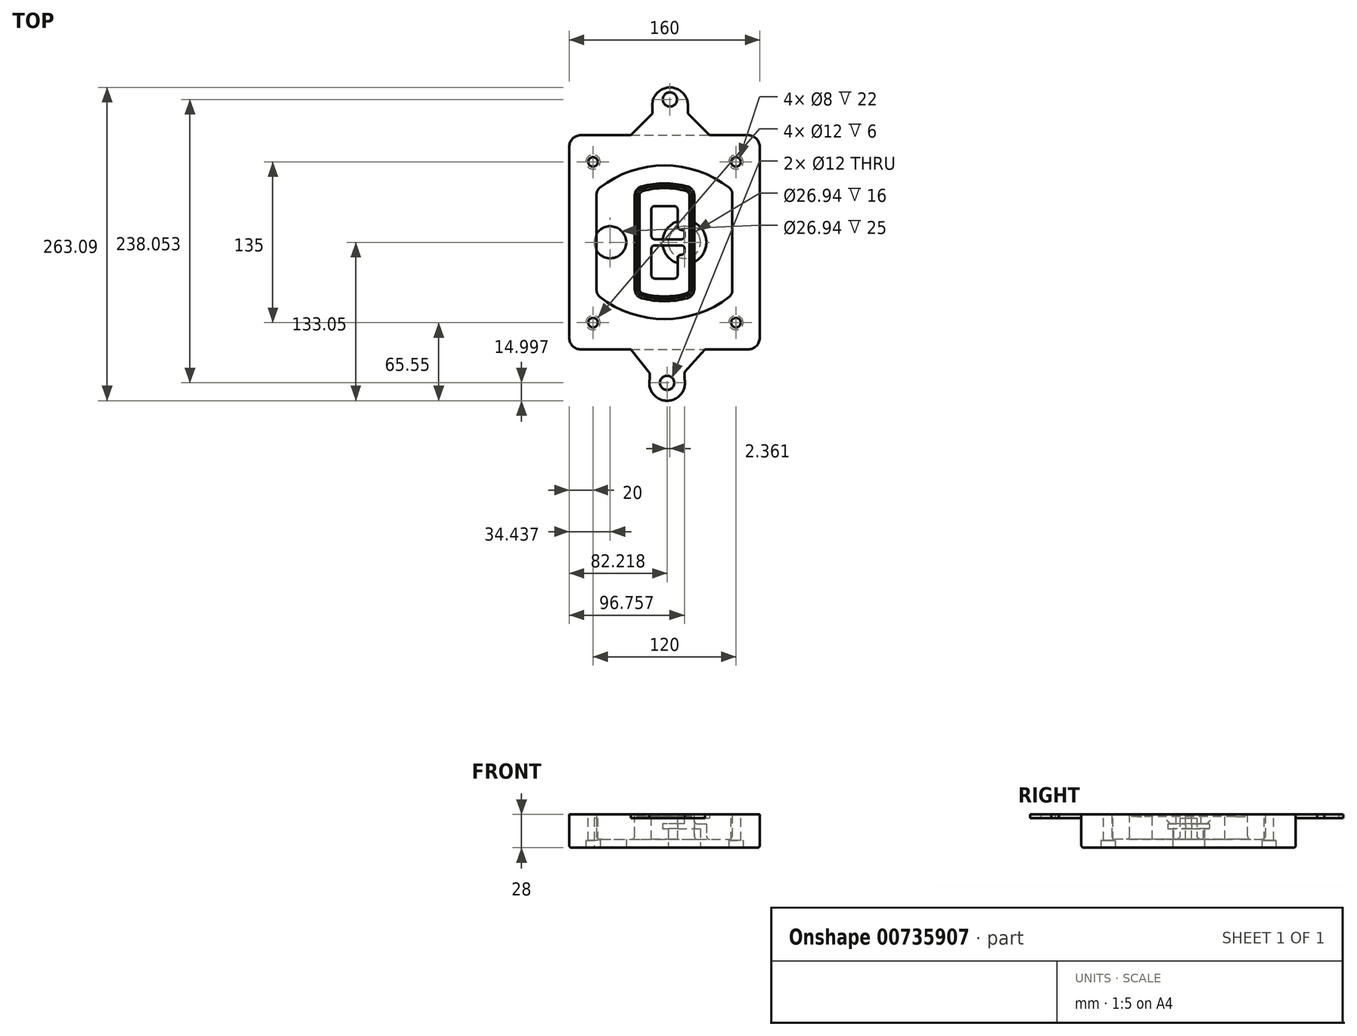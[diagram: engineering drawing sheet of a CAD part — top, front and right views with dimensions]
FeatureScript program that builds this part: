
annotation { "Feature Type Name" : "Feature", "Feature Type Description" : "" }
export const myFeature = defineFeature(function(context is Context, id is Id, definition is map)
    precondition{}
    {
        {
            var Q0;
            Q0=qCreatedBy(makeId("Top.planeOp"),FACE);
            var sketch = newSketch(context, id + "F0", { "sketchPlane" : qUnion([Q0])});
            skPoint(sketch, "E0.rect.middle", {"position": v(0, 0) * mm});
            skLineSegment(sketch, "E1.bottom", {"start": v(-70, -90) * mm, "end": v(70, -90) * mm});
            skLineSegment(sketch, "E1.top", {"start": v(-70, 90) * mm, "end": v(70, 90) * mm});
            skLineSegment(sketch, "E1.left", {"start": v(-80, -80) * mm, "end": v(-80, 80) * mm});
            skLineSegment(sketch, "E1.right", {"start": v(80, -80) * mm, "end": v(80, 80) * mm});
            skLineSegment(sketch, "E2", {"start": v(-80, 90) * mm, "end": v(80, -90) * mm, "construction": true});
            skLineSegment(sketch, "E3", {"start": v(80, 90) * mm, "end": v(-80, -90) * mm, "construction": true});
            skCircle(sketch, "E4", {"center": v(-60, 67.5) * mm, "radius": 4 * mm});
            skCircle(sketch, "E5", {"center": v(60, 67.5) * mm, "radius": 4 * mm});
            skCircle(sketch, "E6", {"center": v(60, -67.5) * mm, "radius": 4 * mm});
            skCircle(sketch, "E7", {"center": v(-60, -67.5) * mm, "radius": 4 * mm});
            skLineSegment(sketch, "E8", {"start": v(-60, 67.5) * mm, "end": v(60, 67.5) * mm, "construction": true});
            skLineSegment(sketch, "E9", {"start": v(60, 67.5) * mm, "end": v(60, -67.5) * mm, "construction": true});
            skLineSegment(sketch, "E10", {"start": v(60, -67.5) * mm, "end": v(-60, -67.5) * mm, "construction": true});
            skLineSegment(sketch, "E11", {"start": v(-60, -67.5) * mm, "end": v(-60, 67.5) * mm, "construction": true});
            skLineSegment(sketch, "E12", {"start": v(-60, 40.3) * mm, "end": v(-60, -40.3) * mm});
            skLineSegment(sketch, "E13", {"start": v(60, 40.3) * mm, "end": v(60, -40.3) * mm});
            skArc(sketch, "E14", {"start": v(56.15, 48.18) * mm, "mid": v(0, 67.5) * mm, "end": v(-56.15, 48.18) * mm});
            skArc(sketch, "E15", {"start": v(-56.15, -48.18) * mm, "mid": v(0, -67.5) * mm, "end": v(56.15, -48.18) * mm});
            skLineSegment(sketch, "E16", {"start": v(-60, 0) * mm, "end": v(60, 0) * mm, "construction": true});
            skPoint(sketch, "E17.visualSharp", {"position": v(-60, -45) * mm});
            skArc(sketch, "E17.filletArc", {"start": v(-60, -40.3) * mm, "mid": v(-58.99, -44.68) * mm, "end": v(-56.15, -48.18) * mm});
            skPoint(sketch, "E18.visualSharp", {"position": v(-60, 45) * mm});
            skArc(sketch, "E18.filletArc", {"start": v(-56.15, 48.18) * mm, "mid": v(-58.99, 44.68) * mm, "end": v(-60, 40.3) * mm});
            skPoint(sketch, "E19.visualSharp", {"position": v(60, 45) * mm});
            skArc(sketch, "E19.filletArc", {"start": v(60, 40.3) * mm, "mid": v(58.99, 44.68) * mm, "end": v(56.15, 48.18) * mm});
            skPoint(sketch, "E20.visualSharp", {"position": v(60, -45) * mm});
            skArc(sketch, "E20.filletArc", {"start": v(56.15, -48.18) * mm, "mid": v(58.99, -44.68) * mm, "end": v(60, -40.3) * mm});
            skPoint(sketch, "E21.visualSharp", {"position": v(-80, 90) * mm});
            skArc(sketch, "E21.filletArc", {"start": v(-70, 90) * mm, "mid": v(-77.07, 87.07) * mm, "end": v(-80, 80) * mm});
            skPoint(sketch, "E22.visualSharp", {"position": v(80, 90) * mm});
            skArc(sketch, "E22.filletArc", {"start": v(80, 80) * mm, "mid": v(77.07, 87.07) * mm, "end": v(70, 90) * mm});
            skPoint(sketch, "E23.visualSharp", {"position": v(80, -90) * mm});
            skArc(sketch, "E23.filletArc", {"start": v(70, -90) * mm, "mid": v(77.07, -87.07) * mm, "end": v(80, -80) * mm});
            skPoint(sketch, "E24.visualSharp", {"position": v(-80, -90) * mm});
            skArc(sketch, "E24.filletArc", {"start": v(-80, -80) * mm, "mid": v(-77.07, -87.07) * mm, "end": v(-70, -90) * mm});
            skArc(sketch, "E25.0", {"start": v(57, 40.3) * mm, "mid": v(56.3, 43.36) * mm, "end": v(54.3, 45.81) * mm});
            skLineSegment(sketch, "E25.1", {"start": v(57, 40.3) * mm, "end": v(57, -40.3) * mm});
            skArc(sketch, "E25.2", {"start": v(54.3, -45.81) * mm, "mid": v(56.3, -43.36) * mm, "end": v(57, -40.3) * mm});
            skArc(sketch, "E25.3", {"start": v(-54.3, -45.81) * mm, "mid": v(0, -64.5) * mm, "end": v(54.3, -45.81) * mm});
            skArc(sketch, "E25.4", {"start": v(-57, -40.3) * mm, "mid": v(-56.3, -43.36) * mm, "end": v(-54.3, -45.81) * mm});
            skArc(sketch, "E25.5", {"start": v(54.3, 45.81) * mm, "mid": v(0, 64.5) * mm, "end": v(-54.3, 45.81) * mm});
            skLineSegment(sketch, "E25.6", {"start": v(-57, 40.3) * mm, "end": v(-57, -40.3) * mm});
            skArc(sketch, "E25.7", {"start": v(-54.3, 45.81) * mm, "mid": v(-56.3, 43.36) * mm, "end": v(-57, 40.3) * mm});
            skArc(sketch, "E26.0", {"start": v(-58.62, 51.33) * mm, "mid": v(-62.58, 46.43) * mm, "end": v(-64, 40.3) * mm});
            skArc(sketch, "E26.1", {"start": v(58.62, 51.33) * mm, "mid": v(0, 71.5) * mm, "end": v(-58.62, 51.33) * mm});
            skArc(sketch, "E26.2", {"start": v(64, 40.3) * mm, "mid": v(62.58, 46.43) * mm, "end": v(58.62, 51.33) * mm});
            skLineSegment(sketch, "E26.3", {"start": v(64, 40.3) * mm, "end": v(64, -40.3) * mm});
            skArc(sketch, "E26.4", {"start": v(58.62, -51.33) * mm, "mid": v(62.58, -46.43) * mm, "end": v(64, -40.3) * mm});
            skLineSegment(sketch, "E26.5", {"start": v(-64, 40.3) * mm, "end": v(-64, -40.3) * mm});
            skArc(sketch, "E26.6", {"start": v(-58.62, -51.33) * mm, "mid": v(0, -71.5) * mm, "end": v(58.62, -51.33) * mm});
            skArc(sketch, "E26.7", {"start": v(-64, -40.3) * mm, "mid": v(-62.58, -46.43) * mm, "end": v(-58.62, -51.33) * mm});
            skSolve(sketch);
        }
        {
            var Q0;
            Q0=makeQuery(id+"F0.imprint","IMPRINT",FACE,{"disambiguationData":[TD([[makeQuery(id+"F0.imprint","IMPRINT",EDGE,{"derivedFrom":sQuery(id+"F0.wireOp",EDGE,"E1.bottom")}),1.0]])]});
            var Q1;
            Q1=makeQuery(id+"F0.imprint","IMPRINT",FACE,{"disambiguationData":[TD([[makeQuery(id+"F0.imprint","IMPRINT",EDGE,{"derivedFrom":sQuery(id+"F0.wireOp",EDGE,"E12")}),1.0]])]});
            var Q2;
            Q2=makeQuery(id+"F0.imprint","IMPRINT",FACE,{"disambiguationData":[TD([[makeQuery(id+"F0.imprint","IMPRINT",EDGE,{"derivedFrom":sQuery(id+"F0.wireOp",EDGE,"E25.0")}),1.0]])]});
            var Q3;
            Q3=makeQuery(id+"F0.imprint","IMPRINT",FACE,{"disambiguationData":[TD([[makeQuery(id+"F0.imprint","IMPRINT",EDGE,{"derivedFrom":sQuery(id+"F0.wireOp",EDGE,"E12")}),-1.0]])]});
            extrude(context, id + "F1", {"entities" : qUnion([Q0, Q1, Q2, Q3]), "oppositeDirection" : true, "depth" : 25 * mm});
        }
        {
            var Q0;
            Q0=makeQuery(id+"F0.imprint","IMPRINT",FACE,{"disambiguationData":[TD([[makeQuery(id+"F0.imprint","IMPRINT",EDGE,{"derivedFrom":sQuery(id+"F0.wireOp",EDGE,"E12")}),1.0]])]});
            extrude(context, id + "F2", {"entities" : qUnion([Q0]), "operationType" : NewBodyOperationType.ADD, "depth" : 3 * mm});
        }
        {
            var Q0;
            Q0=makeQuery(id+"F0.imprint","IMPRINT",FACE,{"disambiguationData":[TD([[makeQuery(id+"F0.imprint","IMPRINT",EDGE,{"derivedFrom":sQuery(id+"F0.wireOp",EDGE,"E25.0")}),1.0]])]});
            extrude(context, id + "F3", {"entities" : qUnion([Q0]), "operationType" : NewBodyOperationType.REMOVE, "oppositeDirection" : true, "depth" : 18 * mm});
        }
        {
            var Q0;
            Q0=makeQuery(id+"F2.opExtrude","CAP_FACE",FACE,{"disambiguationData":[OSD([sQuery(id+"F0.wireOp",EDGE,"E12"),sQuery(id+"F0.wireOp",EDGE,"E13"),sQuery(id+"F0.wireOp",EDGE,"E14"),sQuery(id+"F0.wireOp",EDGE,"E15"),sQuery(id+"F0.wireOp",EDGE,"E17.filletArc"),sQuery(id+"F0.wireOp",EDGE,"E18.filletArc"),sQuery(id+"F0.wireOp",EDGE,"E19.filletArc"),sQuery(id+"F0.wireOp",EDGE,"E20.filletArc"),sQuery(id+"F0.wireOp",EDGE,"E25.0"),sQuery(id+"F0.wireOp",EDGE,"E25.1"),sQuery(id+"F0.wireOp",EDGE,"E25.2"),sQuery(id+"F0.wireOp",EDGE,"E25.3"),sQuery(id+"F0.wireOp",EDGE,"E25.4"),sQuery(id+"F0.wireOp",EDGE,"E25.5"),sQuery(id+"F0.wireOp",EDGE,"E25.6"),sQuery(id+"F0.wireOp",EDGE,"E25.7")])],"isStart":false});
            var sketch = newSketch(context, id + "F4", { "sketchPlane" : qUnion([Q0])});
            skArc(sketch, "E27.0", {"start": v(-19.08, -46.97) * mm, "mid": v(0, -49.5) * mm, "end": v(19.08, -46.97) * mm});
            skArc(sketch, "E28.0", {"start": v(19.08, 46.97) * mm, "mid": v(0, 49.5) * mm, "end": v(-19.08, 46.97) * mm});
            skLineSegment(sketch, "E29", {"start": v(-25, 39.25) * mm, "end": v(-25, -39.25) * mm});
            skLineSegment(sketch, "E30", {"start": v(25, 39.25) * mm, "end": v(25, -39.25) * mm});
            skLineSegment(sketch, "E31", {"start": v(-25, 45.1) * mm, "end": v(25, 45.1) * mm, "construction": true});
            skLineSegment(sketch, "E32", {"start": v(-25, -45.1) * mm, "end": v(25, -45.1) * mm, "construction": true});
            skPoint(sketch, "E33.visualSharp", {"position": v(-25, 45.1) * mm});
            skArc(sketch, "E33.filletArc", {"start": v(-19.08, 46.97) * mm, "mid": v(-23.35, 44.11) * mm, "end": v(-25, 39.25) * mm});
            skPoint(sketch, "E34.visualSharp", {"position": v(25, 45.1) * mm});
            skArc(sketch, "E34.filletArc", {"start": v(25, 39.25) * mm, "mid": v(23.35, 44.11) * mm, "end": v(19.08, 46.97) * mm});
            skPoint(sketch, "E35.visualSharp", {"position": v(25, -45.1) * mm});
            skArc(sketch, "E35.filletArc", {"start": v(19.08, -46.97) * mm, "mid": v(23.35, -44.11) * mm, "end": v(25, -39.25) * mm});
            skPoint(sketch, "E36.visualSharp", {"position": v(-25, -45.1) * mm});
            skArc(sketch, "E36.filletArc", {"start": v(-25, -39.25) * mm, "mid": v(-23.35, -44.11) * mm, "end": v(-19.08, -46.97) * mm});
            skArc(sketch, "E37.0", {"start": v(54.3, 45.81) * mm, "mid": v(0, 64.5) * mm, "end": v(-54.3, 45.81) * mm});
            skArc(sketch, "E37.1", {"start": v(-54.3, 45.81) * mm, "mid": v(-56.3, 43.36) * mm, "end": v(-57, 40.3) * mm});
            skLineSegment(sketch, "E37.2", {"start": v(-57, 40.3) * mm, "end": v(-57, -40.3) * mm});
            skArc(sketch, "E37.3", {"start": v(-57, -40.3) * mm, "mid": v(-56.3, -43.36) * mm, "end": v(-54.3, -45.81) * mm});
            skArc(sketch, "E37.4", {"start": v(-54.3, -45.81) * mm, "mid": v(0, -64.5) * mm, "end": v(54.3, -45.81) * mm});
            skArc(sketch, "E37.5", {"start": v(54.3, -45.81) * mm, "mid": v(56.3, -43.36) * mm, "end": v(57, -40.3) * mm});
            skLineSegment(sketch, "E37.6", {"start": v(57, 40.3) * mm, "end": v(57, -40.3) * mm});
            skArc(sketch, "E37.7", {"start": v(57, 40.3) * mm, "mid": v(56.3, 43.36) * mm, "end": v(54.3, 45.81) * mm});
            skLineSegment(sketch, "E38.0", {"start": v(23, 39.25) * mm, "end": v(23, -39.25) * mm});
            skArc(sketch, "E38.1", {"start": v(18.56, -45.04) * mm, "mid": v(21.76, -42.9) * mm, "end": v(23, -39.25) * mm});
            skArc(sketch, "E38.2", {"start": v(-18.56, -45.04) * mm, "mid": v(0, -47.5) * mm, "end": v(18.56, -45.04) * mm});
            skArc(sketch, "E38.3", {"start": v(-23, -39.25) * mm, "mid": v(-21.76, -42.9) * mm, "end": v(-18.56, -45.04) * mm});
            skLineSegment(sketch, "E38.4", {"start": v(-23, 39.25) * mm, "end": v(-23, -39.25) * mm});
            skArc(sketch, "E38.5", {"start": v(23, 39.25) * mm, "mid": v(21.76, 42.9) * mm, "end": v(18.56, 45.04) * mm});
            skArc(sketch, "E38.6", {"start": v(-18.56, 45.04) * mm, "mid": v(-21.76, 42.9) * mm, "end": v(-23, 39.25) * mm});
            skArc(sketch, "E38.7", {"start": v(18.56, 45.04) * mm, "mid": v(0, 47.5) * mm, "end": v(-18.56, 45.04) * mm});
            skArc(sketch, "E39.0", {"start": v(21, 39.25) * mm, "mid": v(20.18, 41.68) * mm, "end": v(18.04, 43.1) * mm});
            skLineSegment(sketch, "E39.1", {"start": v(21, 39.25) * mm, "end": v(21, -39.25) * mm});
            skArc(sketch, "E39.2", {"start": v(18.04, -43.1) * mm, "mid": v(20.18, -41.68) * mm, "end": v(21, -39.25) * mm});
            skArc(sketch, "E39.3", {"start": v(-18.04, -43.1) * mm, "mid": v(0, -45.5) * mm, "end": v(18.04, -43.1) * mm});
            skArc(sketch, "E39.4", {"start": v(-21, -39.25) * mm, "mid": v(-20.18, -41.68) * mm, "end": v(-18.04, -43.1) * mm});
            skArc(sketch, "E39.5", {"start": v(18.04, 43.1) * mm, "mid": v(0, 45.5) * mm, "end": v(-18.04, 43.1) * mm});
            skLineSegment(sketch, "E39.6", {"start": v(-21, 39.25) * mm, "end": v(-21, -39.25) * mm});
            skArc(sketch, "E39.7", {"start": v(-18.04, 43.1) * mm, "mid": v(-20.18, 41.68) * mm, "end": v(-21, 39.25) * mm});
            skLineSegment(sketch, "E40", {"start": v(-25, 0) * mm, "end": v(25, 0) * mm, "construction": true});
            skLineSegment(sketch, "E41", {"start": v(-11, 5.5) * mm, "end": v(-11, 27.5) * mm});
            skLineSegment(sketch, "E42", {"start": v(-8, 30.5) * mm, "end": v(8, 30.5) * mm});
            skLineSegment(sketch, "E43", {"start": v(11, 27.5) * mm, "end": v(11, 13.5) * mm});
            skLineSegment(sketch, "E44", {"start": v(14, 10.5) * mm, "end": v(14, 10.5) * mm});
            skLineSegment(sketch, "E45", {"start": v(17, 7.5) * mm, "end": v(17, 5.5) * mm});
            skLineSegment(sketch, "E46", {"start": v(14, 2.5) * mm, "end": v(-8, 2.5) * mm});
            skPoint(sketch, "E47.visualSharp", {"position": v(-11, 30.5) * mm});
            skArc(sketch, "E47.filletArc", {"start": v(-8, 30.5) * mm, "mid": v(-10.12, 29.62) * mm, "end": v(-11, 27.5) * mm});
            skPoint(sketch, "E48.visualSharp", {"position": v(11, 30.5) * mm});
            skArc(sketch, "E48.filletArc", {"start": v(11, 27.5) * mm, "mid": v(10.12, 29.62) * mm, "end": v(8, 30.5) * mm});
            skPoint(sketch, "E49.visualSharp", {"position": v(11, 10.5) * mm});
            skArc(sketch, "E49.filletArc", {"start": v(11, 13.5) * mm, "mid": v(11.88, 11.38) * mm, "end": v(14, 10.5) * mm});
            skPoint(sketch, "E50.visualSharp", {"position": v(17, 10.5) * mm});
            skArc(sketch, "E50.filletArc", {"start": v(17, 7.5) * mm, "mid": v(16.12, 9.62) * mm, "end": v(14, 10.5) * mm});
            skPoint(sketch, "E51.visualSharp", {"position": v(17, 2.5) * mm});
            skArc(sketch, "E51.filletArc", {"start": v(14, 2.5) * mm, "mid": v(16.12, 3.38) * mm, "end": v(17, 5.5) * mm});
            skPoint(sketch, "E52.visualSharp", {"position": v(-11, 2.5) * mm});
            skArc(sketch, "E52.filletArc", {"start": v(-11, 5.5) * mm, "mid": v(-10.12, 3.38) * mm, "end": v(-8, 2.5) * mm});
            skLineSegment(sketch, "E53.0.MirrorCS", {"start": v(14, -2.5) * mm, "end": v(-8, -2.5) * mm});
            skArc(sketch, "E54.0.MirrorCS", {"start": v(-11, -5.5) * mm, "mid": v(-10.12, -3.38) * mm, "end": v(-8, -2.5) * mm});
            skLineSegment(sketch, "E55.0.MirrorCS", {"start": v(-11, -5.5) * mm, "end": v(-11, -27.5) * mm});
            skArc(sketch, "E56.0.MirrorCS", {"start": v(-8, -30.5) * mm, "mid": v(-10.12, -29.62) * mm, "end": v(-11, -27.5) * mm});
            skLineSegment(sketch, "E57.0.MirrorCS", {"start": v(-8, -30.5) * mm, "end": v(8, -30.5) * mm});
            skArc(sketch, "E58.0.MirrorCS", {"start": v(11, -27.5) * mm, "mid": v(10.12, -29.62) * mm, "end": v(8, -30.5) * mm});
            skLineSegment(sketch, "E59.0.MirrorCS", {"start": v(11, -27.5) * mm, "end": v(11, -13.5) * mm});
            skArc(sketch, "E60.0.MirrorCS", {"start": v(11, -13.5) * mm, "mid": v(11.88, -11.38) * mm, "end": v(14, -10.5) * mm});
            skArc(sketch, "E61.0.MirrorCS", {"start": v(17, -7.5) * mm, "mid": v(16.12, -9.62) * mm, "end": v(14, -10.5) * mm});
            skLineSegment(sketch, "E62.0.MirrorCS", {"start": v(17, -7.5) * mm, "end": v(17, -5.5) * mm});
            skArc(sketch, "E63.0.MirrorCS", {"start": v(14, -2.5) * mm, "mid": v(16.12, -3.38) * mm, "end": v(17, -5.5) * mm});
            skSolve(sketch);
        }
        {
            var Q0;
            Q0=makeQuery(id+"F4.imprint","IMPRINT",FACE,{"disambiguationData":[TD([[makeQuery(id+"F4.imprint","IMPRINT",EDGE,{"derivedFrom":sQuery(id+"F4.wireOp",EDGE,"E27.0")}),1.0]])]});
            var Q1;
            Q1=makeQuery(id+"F4.imprint","IMPRINT",FACE,{"disambiguationData":[TD([[makeQuery(id+"F4.imprint","IMPRINT",EDGE,{"derivedFrom":sQuery(id+"F4.wireOp",EDGE,"E38.0")}),-1.0]])]});
            var Q2;
            Q2=makeQuery(id+"F4.imprint","IMPRINT",FACE,{"disambiguationData":[TD([[makeQuery(id+"F4.imprint","IMPRINT",EDGE,{"derivedFrom":sQuery(id+"F4.wireOp",EDGE,"E39.0")}),1.0]])]});
            extrude(context, id + "F5", {"entities" : qUnion([Q0, Q1, Q2]), "operationType" : NewBodyOperationType.ADD, "endBound" : BoundingType.UP_TO_NEXT, "oppositeDirection" : true, "depth" : 25 * mm});
        }
        {
            var Q0;
            Q0=makeQuery(id+"F4.imprint","IMPRINT",FACE,{"disambiguationData":[TD([[makeQuery(id+"F4.imprint","IMPRINT",EDGE,{"derivedFrom":sQuery(id+"F4.wireOp",EDGE,"E38.0")}),-1.0]])]});
            extrude(context, id + "F6", {"entities" : qUnion([Q0]), "operationType" : NewBodyOperationType.REMOVE, "oppositeDirection" : true, "depth" : 2 * mm});
        }
        {
            var Q0;
            Q0=makeQuery(id+"F1.opExtrude","CAP_FACE",FACE,{"disambiguationData":[OSD([sQuery(id+"F0.wireOp",EDGE,"E1.bottom"),sQuery(id+"F0.wireOp",EDGE,"E1.top"),sQuery(id+"F0.wireOp",EDGE,"E1.left"),sQuery(id+"F0.wireOp",EDGE,"E1.right"),sQuery(id+"F0.wireOp",EDGE,"E4"),sQuery(id+"F0.wireOp",EDGE,"E5"),sQuery(id+"F0.wireOp",EDGE,"E6"),sQuery(id+"F0.wireOp",EDGE,"E7"),sQuery(id+"F0.wireOp",EDGE,"E21.filletArc"),sQuery(id+"F0.wireOp",EDGE,"E22.filletArc"),sQuery(id+"F0.wireOp",EDGE,"E23.filletArc"),sQuery(id+"F0.wireOp",EDGE,"E24.filletArc")])],"isStart":false});
            var sketch = newSketch(context, id + "F7", { "sketchPlane" : qUnion([Q0])});
            skCircle(sketch, "E64", {"center": v(16.76, 0) * mm, "radius": 13.47 * mm});
            skCircle(sketch, "E65", {"center": v(-45.56, 0) * mm, "radius": 13.47 * mm});
            skLineSegment(sketch, "E66", {"start": v(80, 0) * mm, "end": v(-80, 0) * mm});
            skCircle(sketch, "E67", {"center": v(16.76, 0) * mm, "radius": 18.47 * mm});
            skCircle(sketch, "E68", {"center": v(60, -67.5) * mm, "radius": 6 * mm});
            skCircle(sketch, "E69", {"center": v(-60, -67.5) * mm, "radius": 6 * mm});
            skCircle(sketch, "E70", {"center": v(-60, 67.5) * mm, "radius": 6 * mm});
            skCircle(sketch, "E71", {"center": v(60, 67.5) * mm, "radius": 6 * mm});
            skSolve(sketch);
        }
        {
            var Q0;
            {var subQ1=sQuery(id+"F7.wireOp",EDGE,"E66");var subQ4=sQuery(id+"F7.wireOp",EDGE,"E64");var subQ6=makeQuery(id+"F7.imprint","INTERSECT",VERTEX,{"disambiguationData":[OD(0.0)],"derivedFrom":[subQ4,subQ1]});Q0=makeQuery(id+"F7.imprint","IMPRINT",FACE,{"disambiguationData":[TD([[makeQuery(id+"F7.imprint","IMPRINT",EDGE,{"disambiguationData":[TD([[subQ6,-1.0]])],"derivedFrom":subQ4}),-1.0]])]});}
            var Q1;
            {var subQ0=sQuery(id+"F7.wireOp",EDGE,"E66");var subQ1=sQuery(id+"F7.wireOp",EDGE,"E64");var subQ3=makeQuery(id+"F7.imprint","INTERSECT",VERTEX,{"disambiguationData":[OD(0.0)],"derivedFrom":[subQ1,subQ0]});Q1=makeQuery(id+"F7.imprint","IMPRINT",FACE,{"disambiguationData":[TD([[makeQuery(id+"F7.imprint","IMPRINT",EDGE,{"disambiguationData":[TD([[subQ3,-1.0]])],"derivedFrom":subQ1}),1.0]])]});}
            var Q2;
            {var subQ0=sQuery(id+"F7.wireOp",EDGE,"E66");var subQ1=sQuery(id+"F7.wireOp",EDGE,"E64");var subQ3=makeQuery(id+"F7.imprint","INTERSECT",VERTEX,{"disambiguationData":[OD(0.0)],"derivedFrom":[subQ1,subQ0]});Q2=makeQuery(id+"F7.imprint","IMPRINT",FACE,{"disambiguationData":[TD([[makeQuery(id+"F7.imprint","IMPRINT",EDGE,{"disambiguationData":[TD([[subQ3,1.0]])],"derivedFrom":subQ1}),1.0]])]});}
            var Q3;
            {var subQ1=sQuery(id+"F7.wireOp",EDGE,"E66");var subQ4=sQuery(id+"F7.wireOp",EDGE,"E64");var subQ6=makeQuery(id+"F7.imprint","INTERSECT",VERTEX,{"disambiguationData":[OD(0.0)],"derivedFrom":[subQ4,subQ1]});Q3=makeQuery(id+"F7.imprint","IMPRINT",FACE,{"disambiguationData":[TD([[makeQuery(id+"F7.imprint","IMPRINT",EDGE,{"disambiguationData":[TD([[subQ6,1.0]])],"derivedFrom":subQ4}),-1.0]])]});}
            extrude(context, id + "F8", {"entities" : qUnion([Q0, Q1, Q2, Q3]), "operationType" : NewBodyOperationType.ADD, "oppositeDirection" : true, "depth" : 20 * mm});
        }
        {
            var Q0;
            {var subQ0=sQuery(id+"F7.wireOp",EDGE,"E66");var subQ1=sQuery(id+"F7.wireOp",EDGE,"E64");var subQ3=makeQuery(id+"F7.imprint","INTERSECT",VERTEX,{"disambiguationData":[OD(0.0)],"derivedFrom":[subQ1,subQ0]});Q0=makeQuery(id+"F7.imprint","IMPRINT",FACE,{"disambiguationData":[TD([[makeQuery(id+"F7.imprint","IMPRINT",EDGE,{"disambiguationData":[TD([[subQ3,-1.0]])],"derivedFrom":subQ1}),1.0]])]});}
            var Q1;
            {var subQ0=sQuery(id+"F7.wireOp",EDGE,"E66");var subQ1=sQuery(id+"F7.wireOp",EDGE,"E64");var subQ3=makeQuery(id+"F7.imprint","INTERSECT",VERTEX,{"disambiguationData":[OD(0.0)],"derivedFrom":[subQ1,subQ0]});Q1=makeQuery(id+"F7.imprint","IMPRINT",FACE,{"disambiguationData":[TD([[makeQuery(id+"F7.imprint","IMPRINT",EDGE,{"disambiguationData":[TD([[subQ3,1.0]])],"derivedFrom":subQ1}),1.0]])]});}
            extrude(context, id + "F9", {"entities" : qUnion([Q0, Q1]), "operationType" : NewBodyOperationType.REMOVE, "oppositeDirection" : true, "depth" : 16 * mm});
        }
        {
            var Q0;
            {var subQ0=sQuery(id+"F7.wireOp",EDGE,"E66");var subQ1=sQuery(id+"F7.wireOp",EDGE,"E65");var subQ3=makeQuery(id+"F7.imprint","INTERSECT",VERTEX,{"disambiguationData":[OD(0.0)],"derivedFrom":[subQ1,subQ0]});Q0=makeQuery(id+"F7.imprint","IMPRINT",FACE,{"disambiguationData":[TD([[makeQuery(id+"F7.imprint","IMPRINT",EDGE,{"disambiguationData":[TD([[subQ3,-1.0]])],"derivedFrom":subQ1}),1.0]])]});}
            var Q1;
            {var subQ0=sQuery(id+"F7.wireOp",EDGE,"E66");var subQ1=sQuery(id+"F7.wireOp",EDGE,"E65");var subQ3=makeQuery(id+"F7.imprint","INTERSECT",VERTEX,{"disambiguationData":[OD(0.0)],"derivedFrom":[subQ1,subQ0]});Q1=makeQuery(id+"F7.imprint","IMPRINT",FACE,{"disambiguationData":[TD([[makeQuery(id+"F7.imprint","IMPRINT",EDGE,{"disambiguationData":[TD([[subQ3,1.0]])],"derivedFrom":subQ1}),1.0]])]});}
            extrude(context, id + "F10", {"entities" : qUnion([Q0, Q1]), "operationType" : NewBodyOperationType.REMOVE, "oppositeDirection" : true, "depth" : 25 * mm});
        }
        {
            var Q0;
            Q0=makeQuery(id+"F7.imprint","IMPRINT",FACE,{"disambiguationData":[TD([[makeQuery(id+"F7.imprint","IMPRINT",EDGE,{"derivedFrom":sQuery(id+"F7.wireOp",EDGE,"E68")}),1.0]])]});
            var Q1;
            Q1=makeQuery(id+"F7.imprint","IMPRINT",FACE,{"disambiguationData":[TD([[makeQuery(id+"F7.imprint","IMPRINT",EDGE,{"derivedFrom":makeQuery(id+"F1.opExtrude","CAP_EDGE",EDGE,{"disambiguationData":[OSD([sQuery(id+"F0.wireOp",EDGE,"E5")])],"isStart":false})}),-1.0]])]});
            var Q2;
            Q2=makeQuery(id+"F7.imprint","IMPRINT",FACE,{"disambiguationData":[TD([[makeQuery(id+"F7.imprint","IMPRINT",EDGE,{"derivedFrom":sQuery(id+"F7.wireOp",EDGE,"E69")}),1.0]])]});
            var Q3;
            Q3=makeQuery(id+"F7.imprint","IMPRINT",FACE,{"disambiguationData":[TD([[makeQuery(id+"F7.imprint","IMPRINT",EDGE,{"derivedFrom":makeQuery(id+"F1.opExtrude","CAP_EDGE",EDGE,{"disambiguationData":[OSD([sQuery(id+"F0.wireOp",EDGE,"E4")])],"isStart":false})}),-1.0]])]});
            var Q4;
            Q4=makeQuery(id+"F7.imprint","IMPRINT",FACE,{"disambiguationData":[TD([[makeQuery(id+"F7.imprint","IMPRINT",EDGE,{"derivedFrom":sQuery(id+"F7.wireOp",EDGE,"E70")}),1.0]])]});
            var Q5;
            Q5=makeQuery(id+"F7.imprint","IMPRINT",FACE,{"disambiguationData":[TD([[makeQuery(id+"F7.imprint","IMPRINT",EDGE,{"derivedFrom":makeQuery(id+"F1.opExtrude","CAP_EDGE",EDGE,{"disambiguationData":[OSD([sQuery(id+"F0.wireOp",EDGE,"E7")])],"isStart":false})}),-1.0]])]});
            var Q6;
            Q6=makeQuery(id+"F7.imprint","IMPRINT",FACE,{"disambiguationData":[TD([[makeQuery(id+"F7.imprint","IMPRINT",EDGE,{"derivedFrom":sQuery(id+"F7.wireOp",EDGE,"E71")}),1.0]])]});
            var Q7;
            Q7=makeQuery(id+"F7.imprint","IMPRINT",FACE,{"disambiguationData":[TD([[makeQuery(id+"F7.imprint","IMPRINT",EDGE,{"derivedFrom":makeQuery(id+"F1.opExtrude","CAP_EDGE",EDGE,{"disambiguationData":[OSD([sQuery(id+"F0.wireOp",EDGE,"E6")])],"isStart":false})}),-1.0]])]});
            extrude(context, id + "F11", {"entities" : qUnion([Q0, Q1, Q2, Q3, Q4, Q5, Q6, Q7]), "operationType" : NewBodyOperationType.REMOVE, "oppositeDirection" : true, "depth" : 6 * mm});
        }
        {
            var Q0;
            Q0=makeQuery(id+"F9.boolean.opBoolean","COPY",FACE,{"derivedFrom":makeQuery(id+"F9.opExtrude","CAP_FACE",FACE,{"disambiguationData":[OSD([sQuery(id+"F7.wireOp",EDGE,"E64")])],"isStart":false})});
            var sketch = newSketch(context, id + "F12", { "sketchPlane" : qUnion([Q0])});
            skArc(sketch, "E72.0", {"start": v(11, 17.55) * mm, "mid": v(2.57, 11.82) * mm, "end": v(-1.54, 2.5) * mm});
            skArc(sketch, "E72.1", {"start": v(-1.54, -2.5) * mm, "mid": v(2.57, -11.82) * mm, "end": v(11, -17.55) * mm});
            skLineSegment(sketch, "E73", {"start": v(-1.54, -2.5) * mm, "end": v(14, -2.5) * mm});
            skLineSegment(sketch, "E74.0", {"start": v(14, 2.5) * mm, "end": v(-1.54, 2.5) * mm});
            skArc(sketch, "E74.1", {"start": v(14, 2.5) * mm, "mid": v(16.12, 3.38) * mm, "end": v(17, 5.5) * mm});
            skLineSegment(sketch, "E74.2", {"start": v(17, 7.5) * mm, "end": v(17, 5.5) * mm});
            skArc(sketch, "E74.3", {"start": v(17, 7.5) * mm, "mid": v(16.12, 9.62) * mm, "end": v(14, 10.5) * mm});
            skArc(sketch, "E74.4", {"start": v(11, 13.5) * mm, "mid": v(11.88, 11.38) * mm, "end": v(14, 10.5) * mm});
            skLineSegment(sketch, "E74.5", {"start": v(11, 17.55) * mm, "end": v(11, 13.5) * mm});
            skLineSegment(sketch, "E74.7", {"start": v(14, -2.5) * mm, "end": v(-1.54, -2.5) * mm});
            skArc(sketch, "E74.8", {"start": v(14, -2.5) * mm, "mid": v(16.12, -3.38) * mm, "end": v(17, -5.5) * mm});
            skLineSegment(sketch, "E74.9", {"start": v(17, -7.5) * mm, "end": v(17, -5.5) * mm});
            skArc(sketch, "E74.10", {"start": v(17, -7.5) * mm, "mid": v(16.12, -9.62) * mm, "end": v(14, -10.5) * mm});
            skArc(sketch, "E74.11", {"start": v(11, -13.5) * mm, "mid": v(11.88, -11.38) * mm, "end": v(14, -10.5) * mm});
            skLineSegment(sketch, "E74.12", {"start": v(11, -17.55) * mm, "end": v(11, -13.5) * mm});
            skPoint(sketch, "E75.orphan", {"position": v(11, -27.5) * mm});
            skPoint(sketch, "E76.orphan", {"position": v(-8, -2.5) * mm});
            skPoint(sketch, "E77.orphan", {"position": v(-8, 2.5) * mm});
            skPoint(sketch, "E78.orphan", {"position": v(11, 27.5) * mm});
            skSolve(sketch);
        }
        {
            var Q0;
            {var subQ7=sQuery(id+"F12.wireOp",EDGE,"E72.0");var subQ14=sQuery(id+"F12.wireOp",EDGE,"E72.1");var subQ16=sQuery(id+"F12.wireOp",EDGE,"E74.1");var subQ18=sQuery(id+"F12.wireOp",EDGE,"E74.8");Q0=qUnion([makeQuery(id+"F12.imprint","IMPRINT",FACE,{"disambiguationData":[TD([[makeQuery(id+"F12.imprint","IMPRINT",EDGE,{"derivedFrom":subQ7}),1.0]])]}),makeQuery(id+"F12.imprint","IMPRINT",FACE,{"disambiguationData":[TD([[makeQuery(id+"F12.imprint","IMPRINT",EDGE,{"derivedFrom":subQ14}),1.0]])]}),makeQuery(id+"F12.imprint","IMPRINT",FACE,{"disambiguationData":[TD([[makeQuery(id+"F12.imprint","IMPRINT",EDGE,{"derivedFrom":subQ16}),1.0]])]}),makeQuery(id+"F12.imprint","IMPRINT",FACE,{"disambiguationData":[TD([[makeQuery(id+"F12.imprint","IMPRINT",EDGE,{"derivedFrom":subQ18}),-1.0]])]})]);}
            var Q1;
            Q1=makeQuery(id+"F5.boolean.opBoolean","SPLIT",FACE,{"disambiguationData":[TD([makeQuery(id+"F5.opExtrude","SWEPT_FACE",FACE,{"disambiguationData":[OSD([sQuery(id+"F4.wireOp",EDGE,"E41")])]})])],"derivedFrom":makeQuery(id+"F3.boolean.opBoolean","COPY",FACE,{"derivedFrom":makeQuery(id+"F3.opExtrude","CAP_FACE",FACE,{"disambiguationData":[OSD([sQuery(id+"F0.wireOp",EDGE,"E25.0"),sQuery(id+"F0.wireOp",EDGE,"E25.1"),sQuery(id+"F0.wireOp",EDGE,"E25.2"),sQuery(id+"F0.wireOp",EDGE,"E25.3"),sQuery(id+"F0.wireOp",EDGE,"E25.4"),sQuery(id+"F0.wireOp",EDGE,"E25.5"),sQuery(id+"F0.wireOp",EDGE,"E25.6"),sQuery(id+"F0.wireOp",EDGE,"E25.7")])],"isStart":false})})});
            extrude(context, id + "F13", {"entities" : qUnion([Q0]), "operationType" : NewBodyOperationType.REMOVE, "endBound" : BoundingType.UP_TO_SURFACE, "endBoundEntityFace" : qUnion([Q1]), "depth" : 25 * mm});
        }
        {
            var Q0;
            Q0=makeQuery(id+"F3.boolean.opBoolean","COPY",EDGE,{"derivedFrom":makeQuery(id+"F3.opExtrude","CAP_EDGE",EDGE,{"disambiguationData":[OSD([sQuery(id+"F0.wireOp",EDGE,"E25.6")])],"isStart":false})});
            var Q1;
            Q1=makeQuery(id+"F8.boolean.opBoolean","INTERSECT",EDGE,{"derivedFrom":[makeQuery(id+"F5.opExtrude","SWEPT_FACE",FACE,{"disambiguationData":[OSD([sQuery(id+"F4.wireOp",EDGE,"E30")])]}),makeQuery(id+"F8.opExtrude","CAP_FACE",FACE,{"disambiguationData":[OSD([sQuery(id+"F7.wireOp",EDGE,"E67")])],"isStart":false})]});
            var Q2;
            Q2=makeQuery(id+"F8.boolean.opBoolean","INTERSECT",EDGE,{"disambiguationData":[OD(1.0)],"derivedFrom":[makeQuery(id+"F5.opExtrude","SWEPT_FACE",FACE,{"disambiguationData":[OSD([sQuery(id+"F4.wireOp",EDGE,"E30")])]}),makeQuery(id+"F8.opExtrude","SWEPT_FACE",FACE,{"disambiguationData":[OSD([sQuery(id+"F7.wireOp",EDGE,"E67")])]})]});
            var Q3;
            {var subQ0=sQuery(id+"F4.wireOp",EDGE,"E30");Q3=makeQuery(id+"F8.boolean.opBoolean","SPLIT",EDGE,{"disambiguationData":[TD([makeQuery(id+"F5.opExtrude","SWEPT_FACE",FACE,{"disambiguationData":[OSD([sQuery(id+"F4.wireOp",EDGE,"E35.filletArc")])]})])],"derivedFrom":makeQuery(id+"F5.opExtrude","CAP_EDGE",EDGE,{"disambiguationData":[OSD([subQ0])],"isStart":false})});}
            var Q4;
            {var subQ0=sQuery(id+"F0.wireOp",EDGE,"E25.7");var subQ1=sQuery(id+"F0.wireOp",EDGE,"E25.1");var subQ2=sQuery(id+"F0.wireOp",EDGE,"E25.6");var subQ3=sQuery(id+"F0.wireOp",EDGE,"E25.5");var subQ4=sQuery(id+"F0.wireOp",EDGE,"E25.4");var subQ5=sQuery(id+"F0.wireOp",EDGE,"E25.0");var subQ6=sQuery(id+"F0.wireOp",EDGE,"E25.2");var subQ7=sQuery(id+"F0.wireOp",EDGE,"E25.3");Q4=makeQuery(id+"F8.boolean.opBoolean","INTERSECT",EDGE,{"derivedFrom":[makeQuery(id+"F5.boolean.opBoolean","SPLIT",FACE,{"disambiguationData":[TD([makeQuery(id+"F2.opExtrude","SWEPT_FACE",FACE,{"disambiguationData":[OSD([subQ5])]})])],"derivedFrom":makeQuery(id+"F3.boolean.opBoolean","COPY",FACE,{"derivedFrom":makeQuery(id+"F3.opExtrude","CAP_FACE",FACE,{"disambiguationData":[OSD([subQ5,subQ1,subQ6,subQ7,subQ4,subQ3,subQ2,subQ0])],"isStart":false})})}),makeQuery(id+"F8.opExtrude","SWEPT_FACE",FACE,{"disambiguationData":[OSD([sQuery(id+"F7.wireOp",EDGE,"E67")])]})]});}
            var Q5;
            Q5=makeQuery(id+"F8.boolean.opBoolean","INTERSECT",EDGE,{"disambiguationData":[OD(0.0)],"derivedFrom":[makeQuery(id+"F5.opExtrude","SWEPT_FACE",FACE,{"disambiguationData":[OSD([sQuery(id+"F4.wireOp",EDGE,"E30")])]}),makeQuery(id+"F8.opExtrude","SWEPT_FACE",FACE,{"disambiguationData":[OSD([sQuery(id+"F7.wireOp",EDGE,"E67")])]})]});
            fillet(context, id + "F14", {"entities" : qUnion([Q0, Q1, Q2, Q3, Q4, Q5]), "radius" : 3 * mm, "tangentPropagation" : true, "allowEdgeOverflow" : false});
        }
        {
            var Q0;
            Q0=makeQuery(id+"F1.opExtrude","CAP_EDGE",EDGE,{"disambiguationData":[OSD([sQuery(id+"F0.wireOp",EDGE,"E1.bottom")])],"isStart":false});
            fillet(context, id + "F15", {"entities" : qUnion([Q0]), "radius" : 2 * mm, "tangentPropagation" : true, "allowEdgeOverflow" : false});
        }
        {
            var Q0;
            {var subQ0=sQuery(id+"F0.wireOp",EDGE,"E21.filletArc");var subQ1=sQuery(id+"F0.wireOp",EDGE,"E7");var subQ2=sQuery(id+"F0.wireOp",EDGE,"E6");var subQ3=sQuery(id+"F0.wireOp",EDGE,"E5");var subQ4=sQuery(id+"F0.wireOp",EDGE,"E4");var subQ5=sQuery(id+"F0.wireOp",EDGE,"E22.filletArc");var subQ6=sQuery(id+"F0.wireOp",EDGE,"E1.bottom");var subQ7=sQuery(id+"F0.wireOp",EDGE,"E1.right");var subQ8=sQuery(id+"F0.wireOp",EDGE,"E1.top");var subQ9=sQuery(id+"F0.wireOp",EDGE,"E1.left");var subQ10=sQuery(id+"F0.wireOp",EDGE,"E23.filletArc");var subQ11=sQuery(id+"F0.wireOp",EDGE,"E24.filletArc");Q0=makeQuery(id+"F2.boolean.opBoolean","SPLIT",FACE,{"disambiguationData":[TD([makeQuery(id+"F1.opExtrude","SWEPT_FACE",FACE,{"disambiguationData":[OSD([subQ6])]})])],"derivedFrom":makeQuery(id+"F1.opExtrude","CAP_FACE",FACE,{"disambiguationData":[OSD([subQ6,subQ8,subQ9,subQ7,subQ4,subQ3,subQ2,subQ1,subQ0,subQ5,subQ10,subQ11])],"isStart":true})});}
            var sketch = newSketch(context, id + "F16", { "sketchPlane" : qUnion([Q0])});
            skLineSegment(sketch, "E79", {"start": v(-28.27, 90) * mm, "end": v(-10.27, 108) * mm});
            skLineSegment(sketch, "E80", {"start": v(-10.27, 108) * mm, "end": v(-10.27, 114.07) * mm});
            skLineSegment(sketch, "E81", {"start": v(19.67, 114.15) * mm, "end": v(19.67, 108) * mm});
            skLineSegment(sketch, "E82", {"start": v(19.67, 108) * mm, "end": v(37.67, 90) * mm});
            skArc(sketch, "E83", {"start": v(19.67, 114.15) * mm, "mid": v(4.66, 130.04) * mm, "end": v(-10.27, 114.07) * mm});
            skCircle(sketch, "E84", {"center": v(4.58, 120) * mm, "radius": 6 * mm});
            skPoint(sketch, "E85.end.orphan", {"position": v(80, 0) * mm});
            skPoint(sketch, "E85.start.orphan", {"position": v(-80, 0) * mm});
            skLineSegment(sketch, "E86", {"start": v(-28.27, -90) * mm, "end": v(-12.48, -109.97) * mm});
            skLineSegment(sketch, "E87", {"start": v(-12.48, -109.97) * mm, "end": v(-12.48, -115.08) * mm});
            skPoint(sketch, "E88.end.orphan", {"position": v(37.67, -128.55) * mm});
            skLineSegment(sketch, "E89", {"start": v(16.92, -115.08) * mm, "end": v(16.92, -108.93) * mm});
            skLineSegment(sketch, "E90", {"start": v(16.92, -108.93) * mm, "end": v(33.94, -90) * mm});
            skArc(sketch, "E91", {"start": v(-12.48, -115.08) * mm, "mid": v(2.22, -133.05) * mm, "end": v(16.92, -115.08) * mm});
            skCircle(sketch, "E92", {"center": v(2.22, -118.05) * mm, "radius": 6 * mm});
            skSolve(sketch);
        }
        {
            var Q0;
            Q0=makeQuery(id+"F16.imprint","IMPRINT",FACE,{"disambiguationData":[TD([[makeQuery(id+"F16.imprint","IMPRINT",EDGE,{"derivedFrom":makeQuery(id+"F1.opExtrude","CAP_EDGE",EDGE,{"disambiguationData":[OSD([sQuery(id+"F0.wireOp",EDGE,"E1.left")])],"isStart":true})}),-1.0]])]});
            var Q1;
            {var subQ1=sQuery(id+"F16.wireOp",EDGE,"E79");Q1=makeQuery(id+"F16.imprint","IMPRINT",FACE,{"disambiguationData":[TD([[makeQuery(id+"F16.imprint","IMPRINT",EDGE,{"derivedFrom":subQ1}),-1.0]])]});}
            var Q2;
            {var subQ1=sQuery(id+"F16.wireOp",EDGE,"b3be8f7a-a505-475a-9a49-110dd19488c70.MirrorCS");Q2=makeQuery(id+"F16.imprint","IMPRINT",FACE,{"disambiguationData":[TD([[makeQuery(id+"F16.imprint","IMPRINT",EDGE,{"derivedFrom":subQ1}),1.0]])]});}
            var Q3;
            Q3=makeQuery(id+"F2.opExtrude","CAP_FACE",FACE,{"disambiguationData":[OSD([sQuery(id+"F0.wireOp",EDGE,"E12"),sQuery(id+"F0.wireOp",EDGE,"E13"),sQuery(id+"F0.wireOp",EDGE,"E14"),sQuery(id+"F0.wireOp",EDGE,"E15"),sQuery(id+"F0.wireOp",EDGE,"E17.filletArc"),sQuery(id+"F0.wireOp",EDGE,"E18.filletArc"),sQuery(id+"F0.wireOp",EDGE,"E19.filletArc"),sQuery(id+"F0.wireOp",EDGE,"E20.filletArc"),sQuery(id+"F0.wireOp",EDGE,"E25.0"),sQuery(id+"F0.wireOp",EDGE,"E25.1"),sQuery(id+"F0.wireOp",EDGE,"E25.2"),sQuery(id+"F0.wireOp",EDGE,"E25.3"),sQuery(id+"F0.wireOp",EDGE,"E25.4"),sQuery(id+"F0.wireOp",EDGE,"E25.5"),sQuery(id+"F0.wireOp",EDGE,"E25.6"),sQuery(id+"F0.wireOp",EDGE,"E25.7")])],"isStart":false});
            extrude(context, id + "F17", {"entities" : qUnion([Q0, Q1, Q2]), "endBound" : BoundingType.UP_TO_SURFACE, "depth" : 25 * mm, "endBoundEntityFace" : qUnion([Q3]), "offsetDistance" : 25 * mm});
        }
        {
            var Q0;
            {var subQ1=sQuery(id+"F16.wireOp",EDGE,"E86");Q0=makeQuery(id+"F16.imprint","IMPRINT",FACE,{"disambiguationData":[TD([[makeQuery(id+"F16.imprint","IMPRINT",EDGE,{"derivedFrom":subQ1}),1.0]])]});}
            var Q1;
            Q1=makeQuery(id+"F2.opExtrude","CAP_FACE",FACE,{"disambiguationData":[OSD([sQuery(id+"F0.wireOp",EDGE,"E12"),sQuery(id+"F0.wireOp",EDGE,"E13"),sQuery(id+"F0.wireOp",EDGE,"E14"),sQuery(id+"F0.wireOp",EDGE,"E15"),sQuery(id+"F0.wireOp",EDGE,"E17.filletArc"),sQuery(id+"F0.wireOp",EDGE,"E18.filletArc"),sQuery(id+"F0.wireOp",EDGE,"E19.filletArc"),sQuery(id+"F0.wireOp",EDGE,"E20.filletArc"),sQuery(id+"F0.wireOp",EDGE,"E25.0"),sQuery(id+"F0.wireOp",EDGE,"E25.1"),sQuery(id+"F0.wireOp",EDGE,"E25.2"),sQuery(id+"F0.wireOp",EDGE,"E25.3"),sQuery(id+"F0.wireOp",EDGE,"E25.4"),sQuery(id+"F0.wireOp",EDGE,"E25.5"),sQuery(id+"F0.wireOp",EDGE,"E25.6"),sQuery(id+"F0.wireOp",EDGE,"E25.7")])],"isStart":false});
            extrude(context, id + "F18", {"entities" : qUnion([Q0]), "operationType" : NewBodyOperationType.ADD, "endBound" : BoundingType.UP_TO_SURFACE, "depth" : 25 * mm, "endBoundEntityFace" : qUnion([Q1]), "offsetDistance" : 25 * mm});
        }
    });
